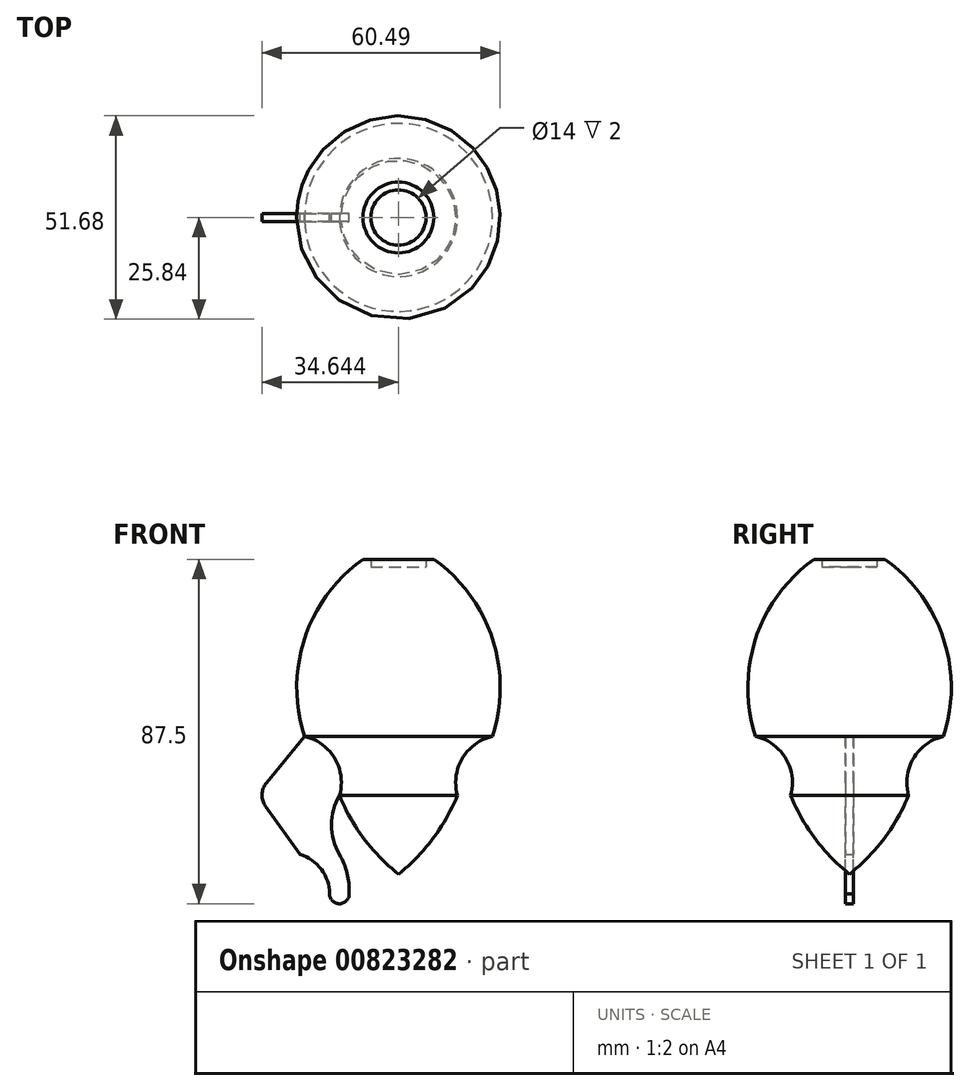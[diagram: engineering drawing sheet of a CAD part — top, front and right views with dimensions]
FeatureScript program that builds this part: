
annotation { "Feature Type Name" : "Feature", "Feature Type Description" : "" }
export const myFeature = defineFeature(function(context is Context, id is Id, definition is map)
    precondition{}
    {
        {
            var Q0;
            Q0=qCreatedBy(makeId("Front.planeOp"),FACE);
            var sketch = newSketch(context, id + "F0", { "sketchPlane" : qUnion([Q0])});
            skLineSegment(sketch, "E0", {"start": v(-30.43, -38.9) * mm, "end": v(-30.43, 41.1) * mm});
            skLineSegment(sketch, "E1", {"start": v(-30.43, 41.1) * mm, "end": v(-21.43, 41.1) * mm});
            skLineSegment(sketch, "E2", {"start": v(-30.43, -3.9) * mm, "end": v(-6.55, -3.9) * mm});
            skLineSegment(sketch, "E3", {"start": v(-30.43, -18.9) * mm, "end": v(-15.43, -18.9) * mm});
            skArc(sketch, "E4", {"start": v(-6.55, -3.9) * mm, "mid": v(-6.6, 21.04) * mm, "end": v(-21.43, 41.1) * mm});
            skArc(sketch, "E5", {"start": v(-30.43, -38.9) * mm, "mid": v(-21.66, -29.85) * mm, "end": v(-15.43, -18.9) * mm});
            skArc(sketch, "E6", {"start": v(-6.55, -3.9) * mm, "mid": v(-14.22, -9.49) * mm, "end": v(-15.43, -18.9) * mm});
            skLineSegment(sketch, "E7.bottom", {"start": v(-30.43, 41.1) * mm, "end": v(-23.43, 41.1) * mm});
            skLineSegment(sketch, "E7.top", {"start": v(-30.43, 39.1) * mm, "end": v(-23.43, 39.1) * mm});
            skLineSegment(sketch, "E7.left", {"start": v(-30.43, 41.1) * mm, "end": v(-30.43, 39.1) * mm});
            skLineSegment(sketch, "E7.right", {"start": v(-23.43, 41.1) * mm, "end": v(-23.43, 39.1) * mm});
            skSolve(sketch);
        }
        {
            var Q0;
            {var subQ1=sQuery(id+"F0.wireOp",EDGE,"E2");Q0=makeQuery(id+"F0.imprint","IMPRINT",FACE,{"disambiguationData":[TD([[makeQuery(id+"F0.imprint","IMPRINT",EDGE,{"derivedFrom":subQ1}),1.0]])]});}
            var Q1;
            {var subQ0=sQuery(id+"F0.wireOp",EDGE,"E2");Q1=makeQuery(id+"F0.imprint","IMPRINT",FACE,{"disambiguationData":[TD([[makeQuery(id+"F0.imprint","IMPRINT",EDGE,{"derivedFrom":subQ0}),-1.0]])]});}
            var Q2;
            {var subQ0=sQuery(id+"F0.wireOp",EDGE,"E3");Q2=makeQuery(id+"F0.imprint","IMPRINT",FACE,{"disambiguationData":[TD([[makeQuery(id+"F0.imprint","IMPRINT",EDGE,{"derivedFrom":subQ0}),-1.0]])]});}
            var Q3;
            Q3=sQuery(id+"F0.wireOp",EDGE,"E0");
            revolve(context, id + "F1", {"surfaceOperationType" : NewSurfaceOperationType.NEW, "entities" : qUnion([Q0, Q1, Q2]), "axis" : qUnion([Q3]), "revolveType" : RevolveType.FULL});
        }
        {
            var Q0;
            Q0=qCreatedBy(makeId("Front.planeOp"),FACE);
            var sketch = newSketch(context, id + "F2", { "sketchPlane" : qUnion([Q0])});
            skLineSegment(sketch, "E8.0", {"start": v(-6.55, -3.9) * mm, "end": v(-54.3, -3.9) * mm});
            skLineSegment(sketch, "E9.0", {"start": v(-15.43, -18.9) * mm, "end": v(-45.43, -18.9) * mm});
            skLineSegment(sketch, "E10", {"start": v(-54.3, -3.9) * mm, "end": v(-45.43, -18.9) * mm});
            skLineSegment(sketch, "E11", {"start": v(-30.43, -3.9) * mm, "end": v(-30.43, -18.9) * mm});
            skLineSegment(sketch, "E12", {"start": v(-30.43, -18.9) * mm, "end": v(-45.43, -18.9) * mm});
            skLineSegment(sketch, "E13", {"start": v(-54.3, -3.9) * mm, "end": v(-30.43, -3.9) * mm});
            skSolve(sketch);
        }
        {
            var Q0;
            {var subQ2=sQuery(id+"F2.wireOp",EDGE,"E10");Q0=makeQuery(id+"F2.imprint","IMPRINT",FACE,{"disambiguationData":[TD([[makeQuery(id+"F2.imprint","IMPRINT",EDGE,{"derivedFrom":subQ2}),1.0]])]});}
            extrude(context, id + "F3", {"entities" : qUnion([Q0]), "operationType" : NewBodyOperationType.ADD, "endBound" : BoundingType.SYMMETRIC, "depth" : 2 * mm, "offsetDistance" : 25 * mm});
        }
        {
            var Q0;
            Q0=qCreatedBy(makeId("Front.planeOp"),FACE);
            var sketch = newSketch(context, id + "F4", { "sketchPlane" : qUnion([Q0])});
            skPoint(sketch, "E14.0", {"position": v(-30.43, -38.9) * mm});
            skLineSegment(sketch, "E15", {"start": v(-30.43, -38.9) * mm, "end": v(-30.43, -43.9) * mm});
            skLineSegment(sketch, "E16", {"start": v(-30.43, -43.9) * mm, "end": v(-45.43, -43.9) * mm});
            skLineSegment(sketch, "E17", {"start": v(-45.43, -43.9) * mm, "end": v(-45.43, -33.9) * mm});
            skLineSegment(sketch, "E18", {"start": v(-45.43, -33.9) * mm, "end": v(-55.43, -33.9) * mm});
            skLineSegment(sketch, "E19", {"start": v(-45.43, -43.9) * mm, "end": v(-47.93, -43.9) * mm});
            skArc(sketch, "E20", {"start": v(-47.93, -43.9) * mm, "mid": v(-45.43, -46.4) * mm, "end": v(-42.93, -43.9) * mm});
            skLineSegment(sketch, "E21.0", {"start": v(-45.4, -18.9) * mm, "end": v(-15.43, -18.9) * mm});
            skArc(sketch, "E22", {"start": v(-45.4, -18.9) * mm, "mid": v(-47.42, -26.4) * mm, "end": v(-45.43, -33.9) * mm});
            skArc(sketch, "E23", {"start": v(-42.93, -43.9) * mm, "mid": v(-43.48, -38.72) * mm, "end": v(-45.43, -33.9) * mm});
            skArc(sketch, "E24", {"start": v(-47.93, -43.9) * mm, "mid": v(-50, -37.65) * mm, "end": v(-55.43, -33.9) * mm});
            skLineSegment(sketch, "E25", {"start": v(-55.43, -33.9) * mm, "end": v(-64.14, -21.74) * mm});
            skLineSegment(sketch, "E26.0", {"start": v(-54.28, -3.9) * mm, "end": v(-6.55, -3.9) * mm});
            skLineSegment(sketch, "E27", {"start": v(-63.94, -15.66) * mm, "end": v(-54.28, -3.9) * mm});
            skPoint(sketch, "E28.visualSharp", {"position": v(-66.37, -18.62) * mm});
            skArc(sketch, "E28.filletArc", {"start": v(-63.94, -15.66) * mm, "mid": v(-65.07, -18.67) * mm, "end": v(-64.14, -21.74) * mm});
            skLineSegment(sketch, "E29", {"start": v(-54.28, -3.9) * mm, "end": v(-45.4, -18.9) * mm});
            skSolve(sketch);
        }
        {
            var Q0;
            Q0=makeQuery(id+"F4.imprint","IMPRINT",FACE,{"disambiguationData":[TD([[makeQuery(id+"F4.imprint","IMPRINT",EDGE,{"derivedFrom":sQuery(id+"F4.wireOp",EDGE,"E18")}),-1.0]])]});
            var Q1;
            Q1=makeQuery(id+"F4.imprint","IMPRINT",FACE,{"disambiguationData":[TD([[makeQuery(id+"F4.imprint","IMPRINT",EDGE,{"derivedFrom":sQuery(id+"F4.wireOp",EDGE,"E17")}),1.0]])]});
            var Q2;
            {var subQ0=sQuery(id+"F4.wireOp",EDGE,"E17");Q2=makeQuery(id+"F4.imprint","IMPRINT",FACE,{"disambiguationData":[TD([[makeQuery(id+"F4.imprint","IMPRINT",EDGE,{"derivedFrom":subQ0}),-1.0]])]});}
            var Q3;
            {var subQ0=sQuery(id+"F4.wireOp",EDGE,"E19");Q3=makeQuery(id+"F4.imprint","IMPRINT",FACE,{"disambiguationData":[TD([[makeQuery(id+"F4.imprint","IMPRINT",EDGE,{"derivedFrom":subQ0}),1.0]])]});}
            extrude(context, id + "F5", {"entities" : qUnion([Q0, Q1, Q2, Q3]), "operationType" : NewBodyOperationType.ADD, "endBound" : BoundingType.SYMMETRIC, "depth" : 2 * mm, "offsetDistance" : 25 * mm});
        }
    });
